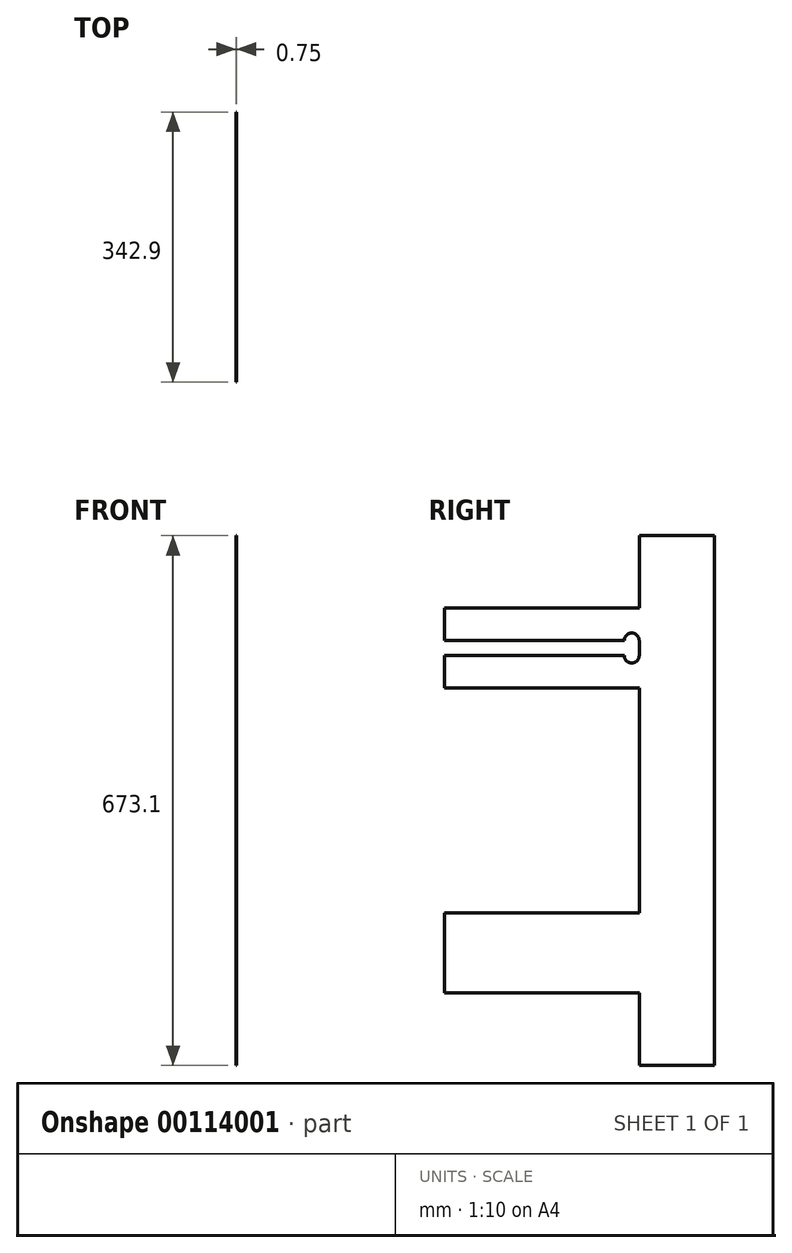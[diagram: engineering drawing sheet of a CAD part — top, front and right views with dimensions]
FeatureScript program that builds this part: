
annotation { "Feature Type Name" : "Feature", "Feature Type Description" : "" }
export const myFeature = defineFeature(function(context is Context, id is Id, definition is map)
    precondition{}
    {
        {
            assignVariable(context, id + "F0", {"name" : "thickness", "anyValue" : 3 / 4});
        }
        {
            var Q0;
            Q0=qCreatedBy(makeId("Right.planeOp"),FACE);
            var sketch = newSketch(context, id + "F1", { "sketchPlane" : qUnion([Q0])});
            skLineSegment(sketch, "E0", {"start": v(-47.63, 0) * mm, "end": v(-47.62, 142.88) * mm});
            skLineSegment(sketch, "E1", {"start": v(-47.62, 142.88) * mm, "end": v(-295.27, 142.87) * mm});
            skLineSegment(sketch, "E2", {"start": v(-295.27, 142.87) * mm, "end": v(-295.27, 244.48) * mm});
            skLineSegment(sketch, "E3", {"start": v(-295.27, 244.48) * mm, "end": v(-47.63, 244.48) * mm});
            skLineSegment(sketch, "E4", {"start": v(-47.62, 244.48) * mm, "end": v(-47.62, 336.55) * mm});
            skLineSegment(sketch, "E5", {"start": v(-47.63, 336.55) * mm, "end": v(47.63, 336.55) * mm});
            skLineSegment(sketch, "E6", {"start": v(47.63, 336.55) * mm, "end": v(47.62, 0) * mm});
            skLineSegment(sketch, "E7", {"start": v(0, 0) * mm, "end": v(-52.97, 0) * mm, "construction": true});
            skLineSegment(sketch, "E8", {"start": v(0, 336.55) * mm, "end": v(0, 0) * mm, "construction": true});
            skLineSegment(sketch, "E9.MirrorCS", {"start": v(-47.62, -142.88) * mm, "end": v(-295.27, -142.88) * mm});
            skLineSegment(sketch, "E10.MirrorCS", {"start": v(-295.27, -142.88) * mm, "end": v(-295.27, -244.48) * mm});
            skLineSegment(sketch, "E11.MirrorCS", {"start": v(-295.27, -244.48) * mm, "end": v(-47.63, -244.48) * mm});
            skLineSegment(sketch, "E12.MirrorCS", {"start": v(-47.63, -244.48) * mm, "end": v(-47.63, -336.55) * mm});
            skLineSegment(sketch, "E13.MirrorCS", {"start": v(-47.63, -336.55) * mm, "end": v(47.63, -336.55) * mm});
            skLineSegment(sketch, "E14.MirrorCS", {"start": v(-47.63, 0) * mm, "end": v(-47.63, -142.88) * mm});
            skLineSegment(sketch, "E15.MirrorCS", {"start": v(47.62, -336.55) * mm, "end": v(47.62, 0) * mm});
            skSolve(sketch);
        }
        {
            var Q0;
            Q0 = qSketchRegion(id + "F1", true);
            extrude(context, id + "F2", {"entities" : qUnion([Q0]), "depth" : (getVariable(context, 'thickness')) * mm});
        }
        {
            var Q0;
            Q0=makeQuery(id+"F2.opExtrude","CAP_FACE",FACE,{"disambiguationData":[OSD([sQuery(id+"F1.wireOp",EDGE,"E0"),sQuery(id+"F1.wireOp",EDGE,"E1"),sQuery(id+"F1.wireOp",EDGE,"E2"),sQuery(id+"F1.wireOp",EDGE,"E3"),sQuery(id+"F1.wireOp",EDGE,"E4"),sQuery(id+"F1.wireOp",EDGE,"E5"),sQuery(id+"F1.wireOp",EDGE,"E6"),sQuery(id+"F1.wireOp",EDGE,"E9.MirrorCS"),sQuery(id+"F1.wireOp",EDGE,"E10.MirrorCS"),sQuery(id+"F1.wireOp",EDGE,"E11.MirrorCS"),sQuery(id+"F1.wireOp",EDGE,"E12.MirrorCS"),sQuery(id+"F1.wireOp",EDGE,"E13.MirrorCS"),sQuery(id+"F1.wireOp",EDGE,"E14.MirrorCS"),sQuery(id+"F1.wireOp",EDGE,"E15.MirrorCS")])],"isStart":false});
            var sketch = newSketch(context, id + "F3", { "sketchPlane" : qUnion([Q0])});
            skLineSegment(sketch, "E16.bottom", {"start": v(-295.27, 203.2) * mm, "end": v(-47.62, 203.2) * mm});
            skLineSegment(sketch, "E16.top", {"start": v(-295.27, 184.15) * mm, "end": v(-47.62, 184.15) * mm});
            skLineSegment(sketch, "E16.left", {"start": v(-295.27, 203.2) * mm, "end": v(-295.27, 184.15) * mm});
            skLineSegment(sketch, "E16.right", {"start": v(-47.62, 203.2) * mm, "end": v(-47.62, 184.15) * mm});
            skLineSegment(sketch, "E17", {"start": v(-47.62, 193.68) * mm, "end": v(-295.27, 193.68) * mm, "construction": true});
            skPoint(sketch, "E18", {"position": v(-295.27, 193.68) * mm});
            skLineSegment(sketch, "E19", {"start": v(0, 0) * mm, "end": v(-105.86, 0) * mm, "construction": true});
            skPoint(sketch, "E19.endSnap0", {"position": v(-47.63, 0) * mm});
            skSolve(sketch);
        }
        {
            var Q0;
            Q0 = qSketchRegion(id + "F3", true);
            extrude(context, id + "F4", {"entities" : qUnion([Q0]), "operationType" : NewBodyOperationType.REMOVE, "oppositeDirection" : true, "depth" : 25.4 * mm});
        }
        {
            var Q0;
            Q0=makeQuery(id+"F2.opExtrude","CAP_FACE",FACE,{"disambiguationData":[OSD([sQuery(id+"F1.wireOp",EDGE,"E0"),sQuery(id+"F1.wireOp",EDGE,"E1"),sQuery(id+"F1.wireOp",EDGE,"E2"),sQuery(id+"F1.wireOp",EDGE,"E3"),sQuery(id+"F1.wireOp",EDGE,"E4"),sQuery(id+"F1.wireOp",EDGE,"E5"),sQuery(id+"F1.wireOp",EDGE,"E6"),sQuery(id+"F1.wireOp",EDGE,"E9.MirrorCS"),sQuery(id+"F1.wireOp",EDGE,"E10.MirrorCS"),sQuery(id+"F1.wireOp",EDGE,"E11.MirrorCS"),sQuery(id+"F1.wireOp",EDGE,"E12.MirrorCS"),sQuery(id+"F1.wireOp",EDGE,"E13.MirrorCS"),sQuery(id+"F1.wireOp",EDGE,"E14.MirrorCS"),sQuery(id+"F1.wireOp",EDGE,"E15.MirrorCS")])],"isStart":false});
            var sketch = newSketch(context, id + "F5", { "sketchPlane" : qUnion([Q0])});
            skArc(sketch, "E20", {"start": v(-47.62, 203.2) * mm, "mid": v(-57.15, 212.73) * mm, "end": v(-66.67, 203.2) * mm});
            skLineSegment(sketch, "E21", {"start": v(-47.62, 193.68) * mm, "end": v(-91.2, 193.68) * mm, "construction": true});
            skArc(sketch, "E22.MirrorCS", {"start": v(-47.62, 184.15) * mm, "mid": v(-57.15, 174.62) * mm, "end": v(-66.67, 184.15) * mm});
            skLineSegment(sketch, "E23", {"start": v(-66.67, 203.2) * mm, "end": v(-66.67, 184.15) * mm});
            skLineSegment(sketch, "E24", {"start": v(-47.62, 203.2) * mm, "end": v(-47.62, 184.15) * mm});
            skLineSegment(sketch, "E25", {"start": v(0, 0) * mm, "end": v(-76.42, 0) * mm, "construction": true});
            skSolve(sketch);
        }
        {
            var Q0;
            Q0 = qSketchRegion(id + "F5", true);
            extrude(context, id + "F6", {"entities" : qUnion([Q0]), "operationType" : NewBodyOperationType.REMOVE, "oppositeDirection" : true, "depth" : 25.4 * mm});
        }
    });
